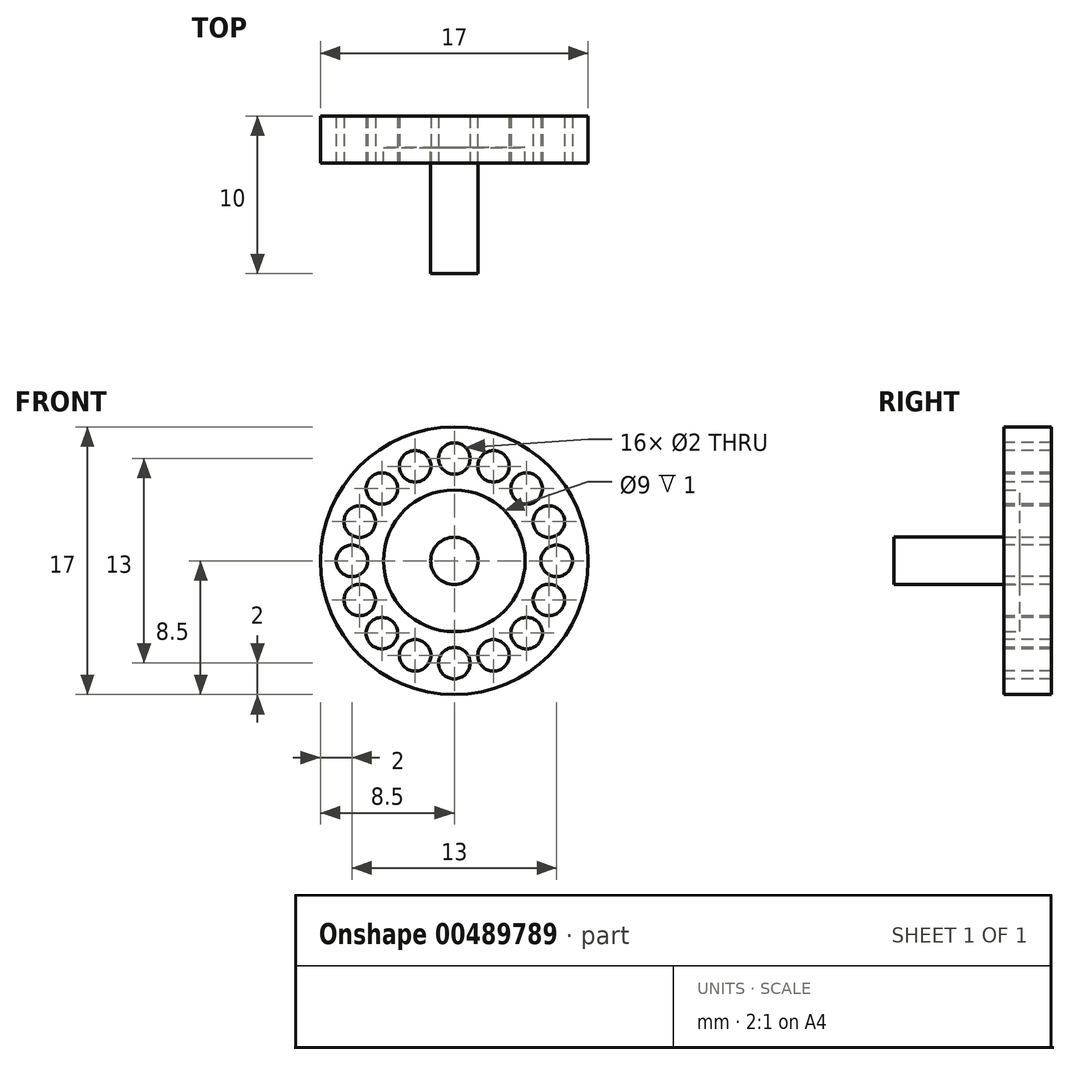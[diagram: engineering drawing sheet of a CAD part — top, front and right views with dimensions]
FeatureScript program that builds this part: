
annotation { "Feature Type Name" : "Feature", "Feature Type Description" : "" }
export const myFeature = defineFeature(function(context is Context, id is Id, definition is map)
    precondition{}
    {
        {
            var Q0;
            Q0=qCreatedBy(makeId("Front.planeOp"),FACE);
            var sketch = newSketch(context, id + "F0", { "sketchPlane" : qUnion([Q0])});
            skCircle(sketch, "E0", {"center": v(0, 0) * mm, "radius": 8.5 * mm});
            skCircle(sketch, "E1", {"center": v(0, 0) * mm, "radius": 4.5 * mm});
            skSolve(sketch);
        }
        {
            var Q0;
            Q0=makeQuery(id+"F0.imprint","IMPRINT",FACE,{"disambiguationData":[TD([[makeQuery(id+"F0.imprint","IMPRINT",EDGE,{"derivedFrom":sQuery(id+"F0.wireOp",EDGE,"E0")}),1.0]])]});
            extrude(context, id + "F1", {"entities" : qUnion([Q0]), "depth" : 3 * mm});
        }
        {
            var Q0;
            Q0=makeQuery(id+"F1.opExtrude","CAP_FACE",FACE,{"disambiguationData":[OSD([sQuery(id+"F0.wireOp",EDGE,"E0"),sQuery(id+"F0.wireOp",EDGE,"E1")])],"isStart":false});
            var sketch = newSketch(context, id + "F2", { "sketchPlane" : qUnion([Q0])});
            skCircle(sketch, "E2", {"center": v(0, 6.5) * mm, "radius": 1 * mm});
            skCircle(sketch, "E3.1.0", {"center": v(-2.49, 6) * mm, "radius": 1 * mm});
            skCircle(sketch, "E3.2.0", {"center": v(-4.6, 4.6) * mm, "radius": 1 * mm});
            skCircle(sketch, "E3.3.0", {"center": v(-6, 2.49) * mm, "radius": 1 * mm});
            skCircle(sketch, "E3.4.0", {"center": v(-6.5, 0) * mm, "radius": 1 * mm});
            skCircle(sketch, "E3.5.0", {"center": v(-6, -2.49) * mm, "radius": 1 * mm});
            skCircle(sketch, "E3.6.0", {"center": v(-4.6, -4.6) * mm, "radius": 1 * mm});
            skCircle(sketch, "E3.7.0", {"center": v(-2.49, -6) * mm, "radius": 1 * mm});
            skCircle(sketch, "E3.8.0", {"center": v(0, -6.5) * mm, "radius": 1 * mm});
            skCircle(sketch, "E3.9.0", {"center": v(2.49, -6) * mm, "radius": 1 * mm});
            skCircle(sketch, "E3.10.0", {"center": v(4.6, -4.6) * mm, "radius": 1 * mm});
            skCircle(sketch, "E3.11.0", {"center": v(6, -2.49) * mm, "radius": 1 * mm});
            skCircle(sketch, "E3.12.0", {"center": v(6.5, 0) * mm, "radius": 1 * mm});
            skCircle(sketch, "E3.13.0", {"center": v(6, 2.49) * mm, "radius": 1 * mm});
            skCircle(sketch, "E3.14.0", {"center": v(4.6, 4.6) * mm, "radius": 1 * mm});
            skCircle(sketch, "E3.15.0", {"center": v(2.49, 6) * mm, "radius": 1 * mm});
            skPoint(sketch, "E3.center", {"position": v(0, 0) * mm});
            skSolve(sketch);
        }
        {
            var Q0;
            Q0=makeQuery(id+"F2.imprint","IMPRINT",FACE,{"disambiguationData":[TD([[makeQuery(id+"F2.imprint","IMPRINT",EDGE,{"derivedFrom":sQuery(id+"F2.wireOp",EDGE,"E2")}),1.0]])]});
            var Q1;
            Q1=makeQuery(id+"F2.imprint","IMPRINT",FACE,{"disambiguationData":[TD([[makeQuery(id+"F2.imprint","IMPRINT",EDGE,{"derivedFrom":sQuery(id+"F2.wireOp",EDGE,"E3.15.0")}),1.0]])]});
            var Q2;
            Q2=makeQuery(id+"F2.imprint","IMPRINT",FACE,{"disambiguationData":[TD([[makeQuery(id+"F2.imprint","IMPRINT",EDGE,{"derivedFrom":sQuery(id+"F2.wireOp",EDGE,"E3.14.0")}),1.0]])]});
            var Q3;
            Q3=makeQuery(id+"F2.imprint","IMPRINT",FACE,{"disambiguationData":[TD([[makeQuery(id+"F2.imprint","IMPRINT",EDGE,{"derivedFrom":sQuery(id+"F2.wireOp",EDGE,"E3.13.0")}),1.0]])]});
            var Q4;
            Q4=makeQuery(id+"F2.imprint","IMPRINT",FACE,{"disambiguationData":[TD([[makeQuery(id+"F2.imprint","IMPRINT",EDGE,{"derivedFrom":sQuery(id+"F2.wireOp",EDGE,"E3.12.0")}),1.0]])]});
            var Q5;
            Q5=makeQuery(id+"F2.imprint","IMPRINT",FACE,{"disambiguationData":[TD([[makeQuery(id+"F2.imprint","IMPRINT",EDGE,{"derivedFrom":sQuery(id+"F2.wireOp",EDGE,"E3.11.0")}),1.0]])]});
            var Q6;
            Q6=makeQuery(id+"F2.imprint","IMPRINT",FACE,{"disambiguationData":[TD([[makeQuery(id+"F2.imprint","IMPRINT",EDGE,{"derivedFrom":sQuery(id+"F2.wireOp",EDGE,"E3.10.0")}),1.0]])]});
            var Q7;
            Q7=makeQuery(id+"F2.imprint","IMPRINT",FACE,{"disambiguationData":[TD([[makeQuery(id+"F2.imprint","IMPRINT",EDGE,{"derivedFrom":sQuery(id+"F2.wireOp",EDGE,"E3.9.0")}),1.0]])]});
            var Q8;
            Q8=makeQuery(id+"F2.imprint","IMPRINT",FACE,{"disambiguationData":[TD([[makeQuery(id+"F2.imprint","IMPRINT",EDGE,{"derivedFrom":sQuery(id+"F2.wireOp",EDGE,"E3.8.0")}),1.0]])]});
            var Q9;
            Q9=makeQuery(id+"F2.imprint","IMPRINT",FACE,{"disambiguationData":[TD([[makeQuery(id+"F2.imprint","IMPRINT",EDGE,{"derivedFrom":sQuery(id+"F2.wireOp",EDGE,"E3.7.0")}),1.0]])]});
            var Q10;
            Q10=makeQuery(id+"F2.imprint","IMPRINT",FACE,{"disambiguationData":[TD([[makeQuery(id+"F2.imprint","IMPRINT",EDGE,{"derivedFrom":sQuery(id+"F2.wireOp",EDGE,"E3.6.0")}),1.0]])]});
            var Q11;
            Q11=makeQuery(id+"F2.imprint","IMPRINT",FACE,{"disambiguationData":[TD([[makeQuery(id+"F2.imprint","IMPRINT",EDGE,{"derivedFrom":sQuery(id+"F2.wireOp",EDGE,"E3.5.0")}),1.0]])]});
            var Q12;
            Q12=makeQuery(id+"F2.imprint","IMPRINT",FACE,{"disambiguationData":[TD([[makeQuery(id+"F2.imprint","IMPRINT",EDGE,{"derivedFrom":sQuery(id+"F2.wireOp",EDGE,"E3.4.0")}),1.0]])]});
            var Q13;
            Q13=makeQuery(id+"F2.imprint","IMPRINT",FACE,{"disambiguationData":[TD([[makeQuery(id+"F2.imprint","IMPRINT",EDGE,{"derivedFrom":sQuery(id+"F2.wireOp",EDGE,"E3.3.0")}),1.0]])]});
            var Q14;
            Q14=makeQuery(id+"F2.imprint","IMPRINT",FACE,{"disambiguationData":[TD([[makeQuery(id+"F2.imprint","IMPRINT",EDGE,{"derivedFrom":sQuery(id+"F2.wireOp",EDGE,"E3.2.0")}),1.0]])]});
            var Q15;
            Q15=makeQuery(id+"F2.imprint","IMPRINT",FACE,{"disambiguationData":[TD([[makeQuery(id+"F2.imprint","IMPRINT",EDGE,{"derivedFrom":sQuery(id+"F2.wireOp",EDGE,"E3.1.0")}),1.0]])]});
            extrude(context, id + "F3", {"entities" : qUnion([Q0, Q1, Q2, Q3, Q4, Q5, Q6, Q7, Q8, Q9, Q10, Q11, Q12, Q13, Q14, Q15]), "operationType" : NewBodyOperationType.REMOVE, "oppositeDirection" : true, "depth" : 5 * mm});
        }
        {
            var Q0;
            Q0=qCreatedBy(makeId("Front.planeOp"),FACE);
            var sketch = newSketch(context, id + "F4", { "sketchPlane" : qUnion([Q0])});
            skCircle(sketch, "E4", {"center": v(0, 0) * mm, "radius": 4.5 * mm});
            skSolve(sketch);
        }
        {
            var Q0;
            Q0=makeQuery(id+"F4.imprint","IMPRINT",FACE,{"disambiguationData":[TD([[makeQuery(id+"F4.imprint","IMPRINT",EDGE,{"derivedFrom":sQuery(id+"F4.wireOp",EDGE,"E4")}),1.0]])]});
            extrude(context, id + "F5", {"entities" : qUnion([Q0]), "operationType" : NewBodyOperationType.ADD, "depth" : 2 * mm});
        }
        {
            var Q0;
            Q0=makeQuery(id+"F5.opExtrude","CAP_FACE",FACE,{"disambiguationData":[OSD([sQuery(id+"F4.wireOp",EDGE,"E4")])],"isStart":false});
            var sketch = newSketch(context, id + "F6", { "sketchPlane" : qUnion([Q0])});
            skCircle(sketch, "E5", {"center": v(0, 0) * mm, "radius": 1.5 * mm});
            skSolve(sketch);
        }
        {
            var Q0;
            Q0=makeQuery(id+"F6.imprint","IMPRINT",FACE,{"disambiguationData":[TD([[makeQuery(id+"F6.imprint","IMPRINT",EDGE,{"derivedFrom":sQuery(id+"F6.wireOp",EDGE,"E5")}),1.0]])]});
            extrude(context, id + "F7", {"entities" : qUnion([Q0]), "operationType" : NewBodyOperationType.ADD, "depth" : 8 * mm});
        }
    });
